# Revit family: Lighting-Pendant-Vibia-BIG_0536
name_source: partatom
category: Lighting Fixtures
revit_build: Autodesk Revit Architecture 2015 (Build: 20140606_1530(x64)
units: mm (PartAtom-declared; Revit-internal decimal feet)

## types (2) — shared parameters
Apparent Load = 120 VA
Cable Material = Metal - VIBIA - Stainless Steel
Color Filter = 16777215
Default Elevation = 50"
Description = BIG exceeds all expectations: it is a light fixture which provides direct ambient down light, achieving a quality akin to a real skylight. Just as the light intensity from a natural skylight changes with the hours of the day the BIG is dimmable creating suitable lighting for a wide range of situations. It is a minimalist expression of fixture design– its white opal methacrylate flat diffuser takes up virtually the entire diameter, with its only flourish a slim chrome band around the outside.
Diffuser Material = Plastic - VIBIA - Light Screen - 2700K
Dimming Lamp Color Temperature Shift = <None>
Emit Shape Visible in Rendering = No
Emit from Circle Diameter = 36"
Lamp Structure Material = Metal - VIBIA - 93 - Matt White Lacquer - RAL 9016
Manufacturer = VIBIA
Number of Poles = 1
Number of poles1 = 1
Photometric Web File = 0536_USA.IES
Power Factor = 0.98
Power Factor1 = 0.98
Product Page URL = http://www.vibia.com
Product data url = https://bimobject.com
Revit Model Version = 3.0
Supply Voltage (277 V max) = 120 V
Tilt Angle = -90.00°
URL = www.vibia.com

## per-type parameters (varying)
| type | Dish Material | Model | Ring Material |
| 0536-01 | Metal - VIBIA - 01 - Polished Chrome | BIG 0536-01 | Metal - VIBIA - 01 - Polished Chrome |
| 0536-93 | Metal - VIBIA - 93 - Matt White Lacquer - RAL 9016 | BIG 0536-93 | Metal - VIBIA - 93 - Matt White Lacquer - RAL 9016 |

## geometry (parser evidence)
native form markers: Sweep x5
no freeform markers — native parametric forms only
